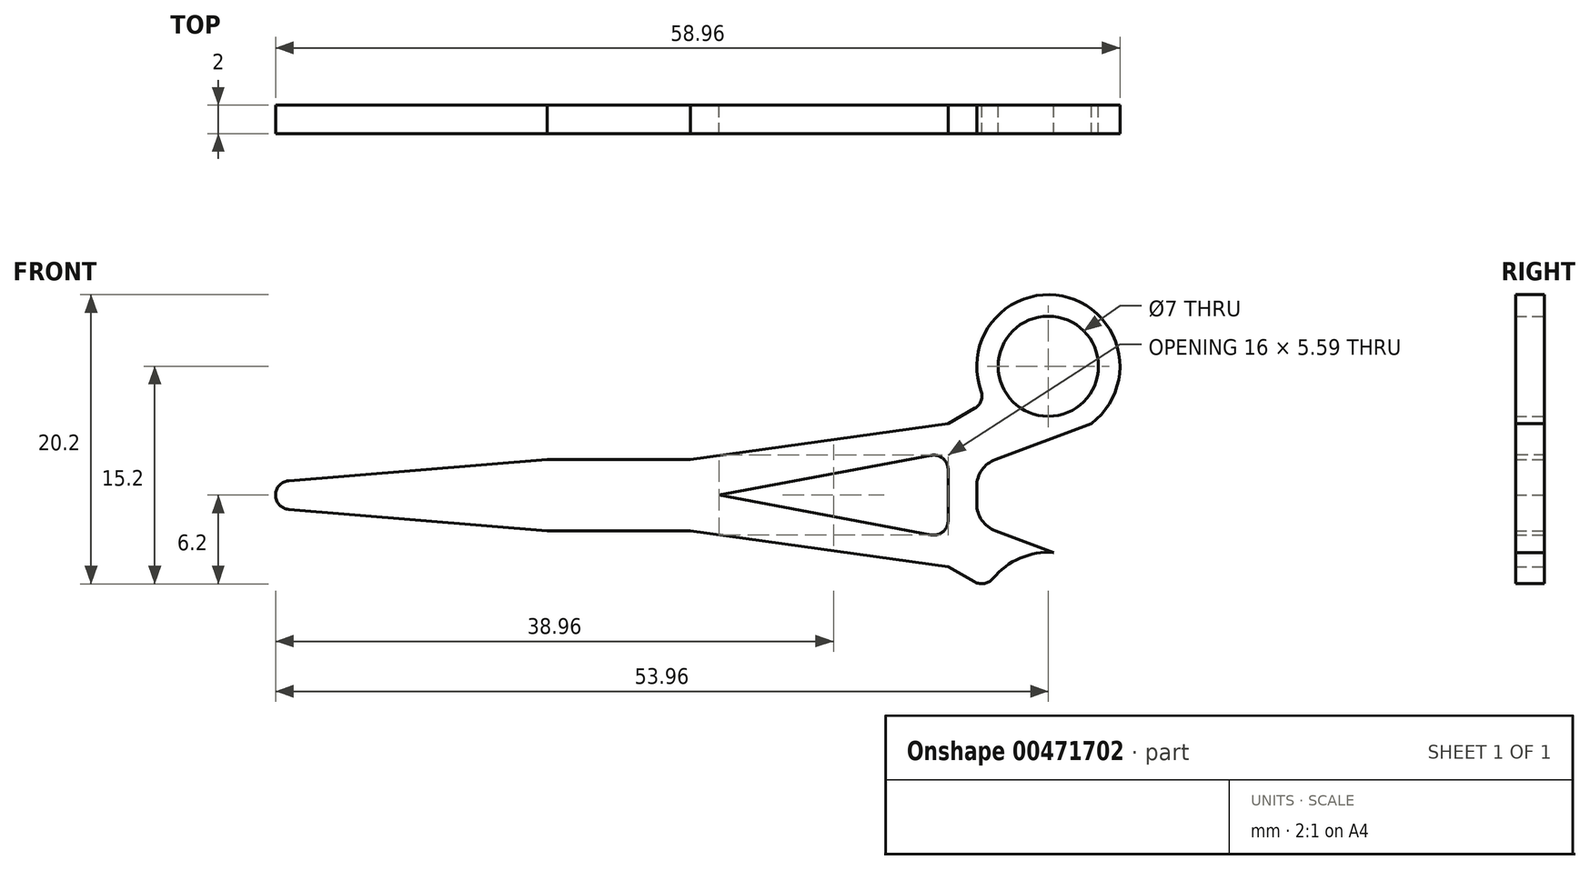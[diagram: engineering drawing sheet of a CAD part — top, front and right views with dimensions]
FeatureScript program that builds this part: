
annotation { "Feature Type Name" : "Feature", "Feature Type Description" : "" }
export const myFeature = defineFeature(function(context is Context, id is Id, definition is map)
    precondition{}
    {
        {
            var Q0;
            Q0=qCreatedBy(makeId("Front.planeOp"),FACE);
            var sketch = newSketch(context, id + "F0", { "sketchPlane" : qUnion([Q0])});
            skLineSegment(sketch, "E0", {"start": v(0, 0) * mm, "end": v(30, 2.5) * mm});
            skLineSegment(sketch, "E1", {"start": v(30, 2.5) * mm, "end": v(40, 2.5) * mm});
            skLineSegment(sketch, "E2", {"start": v(40, 2.5) * mm, "end": v(58, 5) * mm});
            skLineSegment(sketch, "E3", {"start": v(58, 5) * mm, "end": v(65, 9) * mm});
            skCircle(sketch, "E4", {"center": v(65, 9) * mm, "radius": 5 * mm});
            skLineSegment(sketch, "E5", {"start": v(68, 5) * mm, "end": v(60, 2) * mm});
            skLineSegment(sketch, "E6", {"start": v(60, 2) * mm, "end": v(60, 0) * mm});
            skLineSegment(sketch, "E7", {"start": v(60, 0) * mm, "end": v(0, 0) * mm});
            skLineSegment(sketch, "E8.MirrorCS", {"start": v(0, 0) * mm, "end": v(30, -2.5) * mm});
            skLineSegment(sketch, "E9.MirrorCS", {"start": v(30, -2.5) * mm, "end": v(40, -2.5) * mm});
            skLineSegment(sketch, "E10.MirrorCS", {"start": v(40, -2.5) * mm, "end": v(58, -5) * mm});
            skLineSegment(sketch, "E11.MirrorCS", {"start": v(58, -5) * mm, "end": v(65, -9) * mm});
            skCircle(sketch, "E12.MirrorC", {"center": v(65, -9) * mm, "radius": 5 * mm});
            skLineSegment(sketch, "E13.MirrorCS", {"start": v(68, -5) * mm, "end": v(60, -2) * mm});
            skLineSegment(sketch, "E14.MirrorCS", {"start": v(60, -2) * mm, "end": v(60, 0) * mm});
            skLineSegment(sketch, "E15", {"start": v(42, 0) * mm, "end": v(58, 3) * mm});
            skLineSegment(sketch, "E16", {"start": v(58, 3) * mm, "end": v(58, 0) * mm});
            skLineSegment(sketch, "E17.MirrorCS", {"start": v(42, 0) * mm, "end": v(58, -3) * mm});
            skLineSegment(sketch, "E18.MirrorCS", {"start": v(58, -3) * mm, "end": v(58, 0) * mm});
            skCircle(sketch, "E19", {"center": v(65, 9) * mm, "radius": 3.5 * mm});
            skCircle(sketch, "E20.MirrorC", {"center": v(65, -9) * mm, "radius": 3.5 * mm});
            skSolve(sketch);
        }
        {
            var Q0;
            Q0=makeQuery(id+"F0.imprint","IMPRINT",FACE,{"disambiguationData":[TD([[makeQuery(id+"F0.imprint","IMPRINT",EDGE,{"derivedFrom":sQuery(id+"F0.wireOp",EDGE,"E0")}),-1.0]])]});
            var Q1;
            Q1=makeQuery(id+"F0.imprint","IMPRINT",FACE,{"disambiguationData":[TD([[makeQuery(id+"F0.imprint","IMPRINT",EDGE,{"derivedFrom":sQuery(id+"F0.wireOp",EDGE,"E7")}),1.0]])]});
            var Q2;
            {var subQ0=sQuery(id+"F0.wireOp",EDGE,"E4");var subQ1=makeQuery(id+"F0.imprint","INTERSECT",VERTEX,{"derivedFrom":[sQuery(id+"F0.wireOp",EDGE,"E3"),subQ0]});Q2=makeQuery(id+"F0.imprint","IMPRINT",FACE,{"disambiguationData":[TD([[makeQuery(id+"F0.imprint","IMPRINT",EDGE,{"disambiguationData":[TD([[subQ1,-1.0]])],"derivedFrom":subQ0}),1.0]])]});}
            var Q3;
            {var subQ0=sQuery(id+"F0.wireOp",EDGE,"E12.MirrorC");var subQ1=makeQuery(id+"F0.imprint","INTERSECT",VERTEX,{"derivedFrom":[sQuery(id+"F0.wireOp",EDGE,"E11.MirrorCS"),subQ0]});Q3=makeQuery(id+"F0.imprint","IMPRINT",FACE,{"disambiguationData":[TD([[makeQuery(id+"F0.imprint","IMPRINT",EDGE,{"disambiguationData":[TD([[subQ1,-1.0]])],"derivedFrom":subQ0}),-1.0]])]});}
            extrude(context, id + "F1", {"entities" : qUnion([Q0, Q1, Q2, Q3]), "depth" : 2 * mm, "offsetDistance" : 25 * mm});
        }
        {
            var Q0;
            Q0=makeQuery(id+"F1.opExtrude","SWEPT_EDGE",EDGE,{"disambiguationData":[OSD([sQuery(id+"F0.wireOp",EDGE,"E5"),sQuery(id+"F0.wireOp",EDGE,"E6")])]});
            var Q1;
            Q1=makeQuery(id+"F1.opExtrude","SWEPT_EDGE",EDGE,{"disambiguationData":[OSD([sQuery(id+"F0.wireOp",EDGE,"E13.MirrorCS"),sQuery(id+"F0.wireOp",EDGE,"E14.MirrorCS")])]});
            fillet(context, id + "F2", {"entities" : qUnion([Q0, Q1]), "radius" : 2 * mm, "tangentPropagation" : true, "allowEdgeOverflow" : false});
        }
        {
            var Q0;
            Q0=makeQuery(id+"F1.opExtrude","SWEPT_EDGE",EDGE,{"disambiguationData":[OSD([sQuery(id+"F0.wireOp",EDGE,"E15"),sQuery(id+"F0.wireOp",EDGE,"E16")])]});
            var Q1;
            Q1=makeQuery(id+"F1.opExtrude","SWEPT_EDGE",EDGE,{"disambiguationData":[OSD([sQuery(id+"F0.wireOp",EDGE,"E17.MirrorCS"),sQuery(id+"F0.wireOp",EDGE,"E18.MirrorCS")])]});
            var Q2;
            Q2=makeQuery(id+"F1.opExtrude","SWEPT_EDGE",EDGE,{"disambiguationData":[OSD([sQuery(id+"F0.wireOp",EDGE,"E11.MirrorCS"),sQuery(id+"F0.wireOp",EDGE,"E12.MirrorC")])]});
            var Q3;
            Q3=makeQuery(id+"F1.opExtrude","SWEPT_EDGE",EDGE,{"disambiguationData":[OSD([sQuery(id+"F0.wireOp",EDGE,"E3"),sQuery(id+"F0.wireOp",EDGE,"E4")])]});
            var Q4;
            Q4=makeQuery(id+"F1.opExtrude","SWEPT_EDGE",EDGE,{"disambiguationData":[OSD([sQuery(id+"F0.wireOp",EDGE,"E0"),sQuery(id+"F0.wireOp",EDGE,"E7"),sQuery(id+"F0.wireOp",EDGE,"E8.MirrorCS")])]});
            fillet(context, id + "F3", {"entities" : qUnion([Q0, Q1, Q2, Q3, Q4]), "radius" : 1 * mm, "tangentPropagation" : true, "allowEdgeOverflow" : false});
        }
    });
